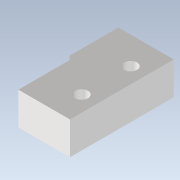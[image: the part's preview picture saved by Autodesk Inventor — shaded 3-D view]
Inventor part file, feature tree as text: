
AUTODESK INVENTOR PART (.ipt)
format: ipt  version: 2022.1 (Build 261234020, 234B)  size: 131,584 bytes
history: native  units: mm
features: sketch x4, extrude x3, fillet x1, hole x1, projected_geometry x1
ambient origin geometry x8: Origin, YZ Plane, XZ Plane, XY Plane, X Axis, Y Axis, Z Axis, Center Point
bodies: Volumenkörper1 (feature_tree)
feature tree (10):
  extrude  "Extrusion1"  Depth=20.1mm
  extrude  "Extrusion2"  Depth=9.96mm
  fillet  "Rundung1"  [1 undecoded]
  hole  "Bohrung1"  [1 undecoded]
  extrude  "Extrusion3"  Depth=1.05mm
  sketch  "Skizze1"  dims[d0=10.7mm d1=20.1mm]
  sketch  "Skizze2"  dims[d2=9.96mm d3=9.9mm d4=45.0deg]
  sketch  "Skizze3"  dims[d5=6.35mm d6=0.0mm d7=2.03mm]
  sketch  "Skizze4"  dims[d8=3.45mm d9=1.05mm d10=1.85mm d11=6.0mm d12=1.6mm d13=0.0mm d14=0.8mm d15=9.5mm d16=6.92mm d17=3.04mm d18=0.0mm d19=5.3mm d20=5.3mm d21=2.5mm d22=6.0mm d23=4.7mm d24=5.2mm d25=90.0deg d26=8.0mm d27=20.594885mm d28=0.2mm d29=1.725mm d30=1.725mm d31=0.43mm d32=0.215mm d33=0.2mm d34=0.0mm]
  projected_geometry  "Projizierte Kontur1"
note: 2 required parameter values undecoded (feature->parameter linkage not recoverable at this tier; creation-order binding heuristic only, values carry confidence <= 0.55)
